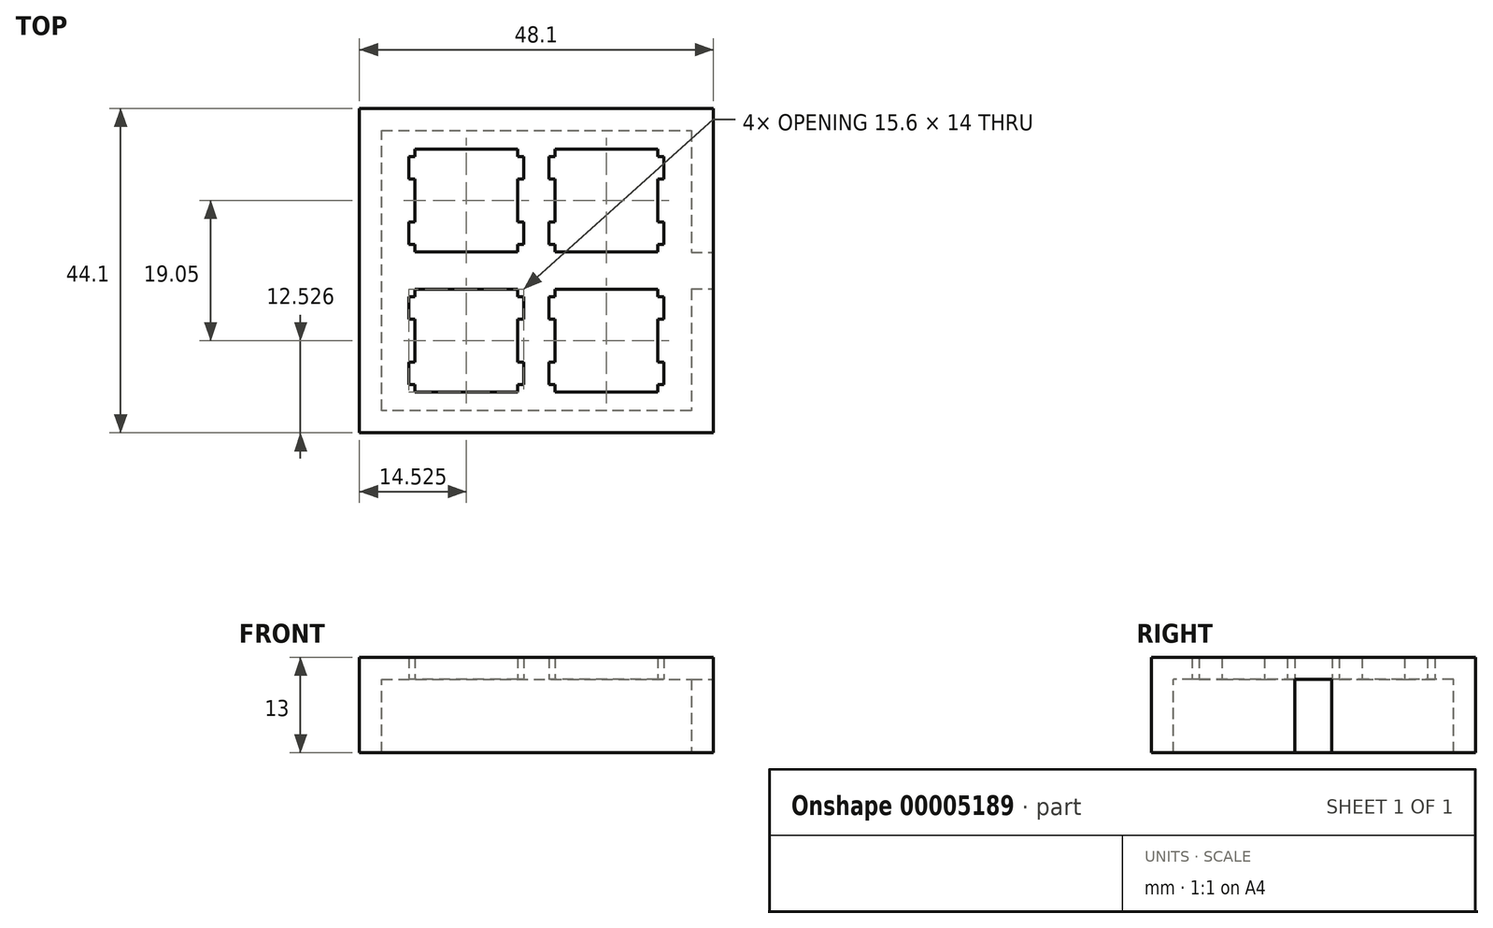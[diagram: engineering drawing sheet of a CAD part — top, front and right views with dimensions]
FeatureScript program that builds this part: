
annotation { "Feature Type Name" : "Feature", "Feature Type Description" : "" }
export const myFeature = defineFeature(function(context is Context, id is Id, definition is map)
    precondition{}
    {
        {
            var Q0;
            Q0=qCreatedBy(makeId("Top.planeOp"),FACE);
            var sketch = newSketch(context, id + "F0", { "sketchPlane" : qUnion([Q0])});
            skLineSegment(sketch, "E0", {"start": v(-21.05, 19.05) * mm, "end": v(21.05, 19.05) * mm});
            skLineSegment(sketch, "E1", {"start": v(21.05, 19.05) * mm, "end": v(21.05, -19.05) * mm});
            skLineSegment(sketch, "E2", {"start": v(21.05, -19.05) * mm, "end": v(-21.05, -19.05) * mm});
            skLineSegment(sketch, "E3", {"start": v(-21.05, -19.05) * mm, "end": v(-21.05, 19.05) * mm});
            skLineSegment(sketch, "E4", {"start": v(-2.53, 3.53) * mm, "end": v(-2.53, 2.53) * mm});
            skLineSegment(sketch, "E5", {"start": v(-2.53, 2.53) * mm, "end": v(-16.52, 2.53) * mm});
            skLineSegment(sketch, "E6", {"start": v(-16.52, 2.53) * mm, "end": v(-16.52, 3.53) * mm});
            skLineSegment(sketch, "E7", {"start": v(-16.52, 3.53) * mm, "end": v(-17.33, 3.53) * mm});
            skLineSegment(sketch, "E8", {"start": v(-17.33, 3.53) * mm, "end": v(-17.33, 6.63) * mm});
            skLineSegment(sketch, "E9", {"start": v(-17.33, 6.63) * mm, "end": v(-16.52, 6.63) * mm});
            skLineSegment(sketch, "E10", {"start": v(-16.52, 6.63) * mm, "end": v(-16.52, 12.42) * mm});
            skLineSegment(sketch, "E11", {"start": v(-16.52, 12.42) * mm, "end": v(-17.33, 12.42) * mm});
            skLineSegment(sketch, "E12", {"start": v(-17.33, 12.42) * mm, "end": v(-17.33, 15.52) * mm});
            skLineSegment(sketch, "E13", {"start": v(-17.33, 15.52) * mm, "end": v(-16.52, 15.52) * mm});
            skLineSegment(sketch, "E14", {"start": v(-16.52, 15.52) * mm, "end": v(-16.52, 16.53) * mm});
            skLineSegment(sketch, "E15", {"start": v(-16.52, 16.53) * mm, "end": v(-2.53, 16.53) * mm});
            skLineSegment(sketch, "E16", {"start": v(-2.53, 16.53) * mm, "end": v(-2.53, 15.52) * mm});
            skLineSegment(sketch, "E17", {"start": v(-2.53, 15.52) * mm, "end": v(-1.72, 15.52) * mm});
            skLineSegment(sketch, "E18", {"start": v(-1.72, 15.52) * mm, "end": v(-1.72, 12.42) * mm});
            skLineSegment(sketch, "E19", {"start": v(-1.72, 12.42) * mm, "end": v(-2.53, 12.42) * mm});
            skLineSegment(sketch, "E20", {"start": v(-2.53, 12.42) * mm, "end": v(-2.53, 6.63) * mm});
            skLineSegment(sketch, "E21", {"start": v(-2.53, 6.63) * mm, "end": v(-1.72, 6.63) * mm});
            skLineSegment(sketch, "E22", {"start": v(-1.72, 6.63) * mm, "end": v(-1.72, 3.53) * mm});
            skLineSegment(sketch, "E23", {"start": v(-1.72, 3.53) * mm, "end": v(-2.53, 3.53) * mm});
            skLineSegment(sketch, "E24", {"start": v(-2.53, -15.52) * mm, "end": v(-2.53, -16.52) * mm});
            skLineSegment(sketch, "E25", {"start": v(-2.53, -16.52) * mm, "end": v(-16.52, -16.52) * mm});
            skLineSegment(sketch, "E26", {"start": v(-16.52, -16.52) * mm, "end": v(-16.52, -15.52) * mm});
            skLineSegment(sketch, "E27", {"start": v(-16.52, -15.52) * mm, "end": v(-17.33, -15.52) * mm});
            skLineSegment(sketch, "E28", {"start": v(-17.33, -15.52) * mm, "end": v(-17.33, -12.42) * mm});
            skLineSegment(sketch, "E29", {"start": v(-17.33, -12.42) * mm, "end": v(-16.52, -12.42) * mm});
            skLineSegment(sketch, "E30", {"start": v(-16.52, -12.42) * mm, "end": v(-16.52, -6.63) * mm});
            skLineSegment(sketch, "E31", {"start": v(-16.52, -6.63) * mm, "end": v(-17.33, -6.63) * mm});
            skLineSegment(sketch, "E32", {"start": v(-17.33, -6.63) * mm, "end": v(-17.33, -3.53) * mm});
            skLineSegment(sketch, "E33", {"start": v(-17.33, -3.53) * mm, "end": v(-16.52, -3.53) * mm});
            skLineSegment(sketch, "E34", {"start": v(-16.52, -3.53) * mm, "end": v(-16.52, -2.52) * mm});
            skLineSegment(sketch, "E35", {"start": v(-16.52, -2.52) * mm, "end": v(-2.53, -2.52) * mm});
            skLineSegment(sketch, "E36", {"start": v(-2.53, -2.52) * mm, "end": v(-2.53, -3.53) * mm});
            skLineSegment(sketch, "E37", {"start": v(-2.53, -3.53) * mm, "end": v(-1.72, -3.53) * mm});
            skLineSegment(sketch, "E38", {"start": v(-1.72, -3.53) * mm, "end": v(-1.72, -6.63) * mm});
            skLineSegment(sketch, "E39", {"start": v(-1.72, -6.63) * mm, "end": v(-2.53, -6.63) * mm});
            skLineSegment(sketch, "E40", {"start": v(-2.53, -6.63) * mm, "end": v(-2.53, -12.42) * mm});
            skLineSegment(sketch, "E41", {"start": v(-2.53, -12.42) * mm, "end": v(-1.72, -12.42) * mm});
            skLineSegment(sketch, "E42", {"start": v(-1.72, -12.42) * mm, "end": v(-1.72, -15.52) * mm});
            skLineSegment(sketch, "E43", {"start": v(-1.72, -15.52) * mm, "end": v(-2.53, -15.52) * mm});
            skLineSegment(sketch, "E44", {"start": v(16.52, 3.53) * mm, "end": v(16.52, 2.53) * mm});
            skLineSegment(sketch, "E45", {"start": v(16.52, 2.53) * mm, "end": v(2.53, 2.53) * mm});
            skLineSegment(sketch, "E46", {"start": v(2.53, 2.53) * mm, "end": v(2.53, 3.53) * mm});
            skLineSegment(sketch, "E47", {"start": v(2.53, 3.53) * mm, "end": v(1.72, 3.53) * mm});
            skLineSegment(sketch, "E48", {"start": v(1.72, 3.53) * mm, "end": v(1.72, 6.63) * mm});
            skLineSegment(sketch, "E49", {"start": v(1.72, 6.63) * mm, "end": v(2.53, 6.63) * mm});
            skLineSegment(sketch, "E50", {"start": v(2.53, 6.63) * mm, "end": v(2.53, 12.42) * mm});
            skLineSegment(sketch, "E51", {"start": v(2.53, 12.42) * mm, "end": v(1.72, 12.42) * mm});
            skLineSegment(sketch, "E52", {"start": v(1.72, 12.42) * mm, "end": v(1.72, 15.52) * mm});
            skLineSegment(sketch, "E53", {"start": v(1.72, 15.52) * mm, "end": v(2.53, 15.52) * mm});
            skLineSegment(sketch, "E54", {"start": v(2.53, 15.52) * mm, "end": v(2.53, 16.53) * mm});
            skLineSegment(sketch, "E55", {"start": v(2.53, 16.53) * mm, "end": v(16.52, 16.53) * mm});
            skLineSegment(sketch, "E56", {"start": v(16.52, 16.53) * mm, "end": v(16.52, 15.52) * mm});
            skLineSegment(sketch, "E57", {"start": v(16.52, 15.52) * mm, "end": v(17.33, 15.52) * mm});
            skLineSegment(sketch, "E58", {"start": v(17.33, 15.52) * mm, "end": v(17.33, 12.42) * mm});
            skLineSegment(sketch, "E59", {"start": v(17.33, 12.42) * mm, "end": v(16.52, 12.42) * mm});
            skLineSegment(sketch, "E60", {"start": v(16.52, 12.42) * mm, "end": v(16.52, 6.63) * mm});
            skLineSegment(sketch, "E61", {"start": v(16.52, 6.63) * mm, "end": v(17.33, 6.63) * mm});
            skLineSegment(sketch, "E62", {"start": v(17.33, 6.63) * mm, "end": v(17.33, 3.53) * mm});
            skLineSegment(sketch, "E63", {"start": v(17.33, 3.53) * mm, "end": v(16.52, 3.53) * mm});
            skLineSegment(sketch, "E64", {"start": v(16.52, -15.52) * mm, "end": v(16.52, -16.52) * mm});
            skLineSegment(sketch, "E65", {"start": v(16.52, -16.52) * mm, "end": v(2.53, -16.52) * mm});
            skLineSegment(sketch, "E66", {"start": v(2.53, -16.52) * mm, "end": v(2.53, -15.52) * mm});
            skLineSegment(sketch, "E67", {"start": v(2.53, -15.52) * mm, "end": v(1.72, -15.52) * mm});
            skLineSegment(sketch, "E68", {"start": v(1.72, -15.52) * mm, "end": v(1.72, -12.42) * mm});
            skLineSegment(sketch, "E69", {"start": v(1.72, -12.42) * mm, "end": v(2.53, -12.42) * mm});
            skLineSegment(sketch, "E70", {"start": v(2.53, -12.42) * mm, "end": v(2.53, -6.63) * mm});
            skLineSegment(sketch, "E71", {"start": v(2.53, -6.63) * mm, "end": v(1.72, -6.63) * mm});
            skLineSegment(sketch, "E72", {"start": v(1.72, -6.63) * mm, "end": v(1.72, -3.53) * mm});
            skLineSegment(sketch, "E73", {"start": v(1.72, -3.53) * mm, "end": v(2.53, -3.53) * mm});
            skLineSegment(sketch, "E74", {"start": v(2.53, -3.53) * mm, "end": v(2.53, -2.52) * mm});
            skLineSegment(sketch, "E75", {"start": v(2.53, -2.52) * mm, "end": v(16.52, -2.52) * mm});
            skLineSegment(sketch, "E76", {"start": v(16.52, -2.52) * mm, "end": v(16.52, -3.53) * mm});
            skLineSegment(sketch, "E77", {"start": v(16.52, -3.53) * mm, "end": v(17.33, -3.53) * mm});
            skLineSegment(sketch, "E78", {"start": v(17.33, -3.53) * mm, "end": v(17.33, -6.63) * mm});
            skLineSegment(sketch, "E79", {"start": v(17.33, -6.63) * mm, "end": v(16.52, -6.63) * mm});
            skLineSegment(sketch, "E80", {"start": v(16.52, -6.63) * mm, "end": v(16.52, -12.42) * mm});
            skLineSegment(sketch, "E81", {"start": v(16.52, -12.42) * mm, "end": v(17.33, -12.42) * mm});
            skLineSegment(sketch, "E82", {"start": v(17.33, -12.42) * mm, "end": v(17.33, -15.52) * mm});
            skLineSegment(sketch, "E83", {"start": v(17.33, -15.52) * mm, "end": v(16.52, -15.52) * mm});
            skSolve(sketch);
        }
        {
            var Q0;
            Q0 = qSketchRegion(id + "F0", true);
            extrude(context, id + "F1", {"entities" : qUnion([Q0]), "depth" : 3 * mm});
        }
        {
            var Q0;
            Q0=makeQuery(id+"F1.opExtrude","CAP_FACE",FACE,{"disambiguationData":[OSD([sQuery(id+"F0.wireOp",EDGE,"E0"),sQuery(id+"F0.wireOp",EDGE,"E1"),sQuery(id+"F0.wireOp",EDGE,"E2"),sQuery(id+"F0.wireOp",EDGE,"E3"),sQuery(id+"F0.wireOp",EDGE,"E4"),sQuery(id+"F0.wireOp",EDGE,"E5"),sQuery(id+"F0.wireOp",EDGE,"E6"),sQuery(id+"F0.wireOp",EDGE,"E7"),sQuery(id+"F0.wireOp",EDGE,"E8"),sQuery(id+"F0.wireOp",EDGE,"E9"),sQuery(id+"F0.wireOp",EDGE,"E10"),sQuery(id+"F0.wireOp",EDGE,"E11"),sQuery(id+"F0.wireOp",EDGE,"E12"),sQuery(id+"F0.wireOp",EDGE,"E13"),sQuery(id+"F0.wireOp",EDGE,"E14"),sQuery(id+"F0.wireOp",EDGE,"E15"),sQuery(id+"F0.wireOp",EDGE,"E16"),sQuery(id+"F0.wireOp",EDGE,"E17"),sQuery(id+"F0.wireOp",EDGE,"E18"),sQuery(id+"F0.wireOp",EDGE,"E19"),sQuery(id+"F0.wireOp",EDGE,"E20"),sQuery(id+"F0.wireOp",EDGE,"E21"),sQuery(id+"F0.wireOp",EDGE,"E22"),sQuery(id+"F0.wireOp",EDGE,"E23"),sQuery(id+"F0.wireOp",EDGE,"E24"),sQuery(id+"F0.wireOp",EDGE,"E25"),sQuery(id+"F0.wireOp",EDGE,"E26"),sQuery(id+"F0.wireOp",EDGE,"E27"),sQuery(id+"F0.wireOp",EDGE,"E28"),sQuery(id+"F0.wireOp",EDGE,"E29"),sQuery(id+"F0.wireOp",EDGE,"E30"),sQuery(id+"F0.wireOp",EDGE,"E31"),sQuery(id+"F0.wireOp",EDGE,"E32"),sQuery(id+"F0.wireOp",EDGE,"E33"),sQuery(id+"F0.wireOp",EDGE,"E34"),sQuery(id+"F0.wireOp",EDGE,"E35"),sQuery(id+"F0.wireOp",EDGE,"E36"),sQuery(id+"F0.wireOp",EDGE,"E37"),sQuery(id+"F0.wireOp",EDGE,"E38"),sQuery(id+"F0.wireOp",EDGE,"E39"),sQuery(id+"F0.wireOp",EDGE,"E40"),sQuery(id+"F0.wireOp",EDGE,"E41"),sQuery(id+"F0.wireOp",EDGE,"E42"),sQuery(id+"F0.wireOp",EDGE,"E43"),sQuery(id+"F0.wireOp",EDGE,"E44"),sQuery(id+"F0.wireOp",EDGE,"E45"),sQuery(id+"F0.wireOp",EDGE,"E46"),sQuery(id+"F0.wireOp",EDGE,"E47"),sQuery(id+"F0.wireOp",EDGE,"E48"),sQuery(id+"F0.wireOp",EDGE,"E49"),sQuery(id+"F0.wireOp",EDGE,"E50"),sQuery(id+"F0.wireOp",EDGE,"E51"),sQuery(id+"F0.wireOp",EDGE,"E52"),sQuery(id+"F0.wireOp",EDGE,"E53"),sQuery(id+"F0.wireOp",EDGE,"E54"),sQuery(id+"F0.wireOp",EDGE,"E55"),sQuery(id+"F0.wireOp",EDGE,"E56"),sQuery(id+"F0.wireOp",EDGE,"E57"),sQuery(id+"F0.wireOp",EDGE,"E58"),sQuery(id+"F0.wireOp",EDGE,"E59"),sQuery(id+"F0.wireOp",EDGE,"E60"),sQuery(id+"F0.wireOp",EDGE,"E61"),sQuery(id+"F0.wireOp",EDGE,"E62"),sQuery(id+"F0.wireOp",EDGE,"E63"),sQuery(id+"F0.wireOp",EDGE,"E64"),sQuery(id+"F0.wireOp",EDGE,"E65"),sQuery(id+"F0.wireOp",EDGE,"E66"),sQuery(id+"F0.wireOp",EDGE,"E67"),sQuery(id+"F0.wireOp",EDGE,"E68"),sQuery(id+"F0.wireOp",EDGE,"E69"),sQuery(id+"F0.wireOp",EDGE,"E70"),sQuery(id+"F0.wireOp",EDGE,"E71"),sQuery(id+"F0.wireOp",EDGE,"E72"),sQuery(id+"F0.wireOp",EDGE,"E73"),sQuery(id+"F0.wireOp",EDGE,"E74"),sQuery(id+"F0.wireOp",EDGE,"E75"),sQuery(id+"F0.wireOp",EDGE,"E76"),sQuery(id+"F0.wireOp",EDGE,"E77"),sQuery(id+"F0.wireOp",EDGE,"E78"),sQuery(id+"F0.wireOp",EDGE,"E79"),sQuery(id+"F0.wireOp",EDGE,"E80"),sQuery(id+"F0.wireOp",EDGE,"E81"),sQuery(id+"F0.wireOp",EDGE,"E82"),sQuery(id+"F0.wireOp",EDGE,"E83")])],"isStart":false});
            var sketch = newSketch(context, id + "F2", { "sketchPlane" : qUnion([Q0])});
            skLineSegment(sketch, "E84.0", {"start": v(-21.05, 19.05) * mm, "end": v(21.05, 19.05) * mm});
            skLineSegment(sketch, "E84.1", {"start": v(-21.05, -19.05) * mm, "end": v(-21.05, 19.05) * mm});
            skLineSegment(sketch, "E84.2", {"start": v(21.05, -19.05) * mm, "end": v(-21.05, -19.05) * mm});
            skLineSegment(sketch, "E84.3", {"start": v(21.05, 19.05) * mm, "end": v(21.05, -19.05) * mm});
            skLineSegment(sketch, "E85.0", {"start": v(-24.05, 22.05) * mm, "end": v(24.05, 22.05) * mm});
            skLineSegment(sketch, "E85.1", {"start": v(-24.05, -22.05) * mm, "end": v(-24.05, 22.05) * mm});
            skLineSegment(sketch, "E85.2", {"start": v(24.05, -22.05) * mm, "end": v(-24.05, -22.05) * mm});
            skLineSegment(sketch, "E85.3", {"start": v(24.05, 22.05) * mm, "end": v(24.05, -22.05) * mm});
            skSolve(sketch);
        }
        {
            var Q0;
            Q0 = qSketchRegion(id + "F2", true);
            extrude(context, id + "F3", {"entities" : qUnion([Q0]), "operationType" : NewBodyOperationType.ADD, "oppositeDirection" : true, "depth" : 13 * mm});
        }
        {
            var Q0;
            Q0=makeQuery(id+"F3.opExtrude","SWEPT_FACE",FACE,{"disambiguationData":[OSD([sQuery(id+"F2.wireOp",EDGE,"E85.3")])]});
            var sketch = newSketch(context, id + "F4", { "sketchPlane" : qUnion([Q0])});
            skLineSegment(sketch, "E86.0", {"start": v(19.05, 0) * mm, "end": v(-19.05, 0) * mm, "construction": true});
            skLineSegment(sketch, "E87", {"start": v(0, 0) * mm, "end": v(0, -10) * mm, "construction": true});
            skLineSegment(sketch, "E88.bottom", {"start": v(-2.5, 0) * mm, "end": v(2.5, 0) * mm});
            skLineSegment(sketch, "E88.top", {"start": v(-2.5, -10) * mm, "end": v(2.5, -10) * mm});
            skLineSegment(sketch, "E88.left", {"start": v(-2.5, 0) * mm, "end": v(-2.5, -10) * mm});
            skLineSegment(sketch, "E88.right", {"start": v(2.5, 0) * mm, "end": v(2.5, -10) * mm});
            skSolve(sketch);
        }
        {
            var Q0;
            Q0 = qSketchRegion(id + "F4", true);
            extrude(context, id + "F5", {"entities" : qUnion([Q0]), "operationType" : NewBodyOperationType.REMOVE, "endBound" : BoundingType.UP_TO_NEXT, "oppositeDirection" : true, "depth" : 25 * mm});
        }
    });
